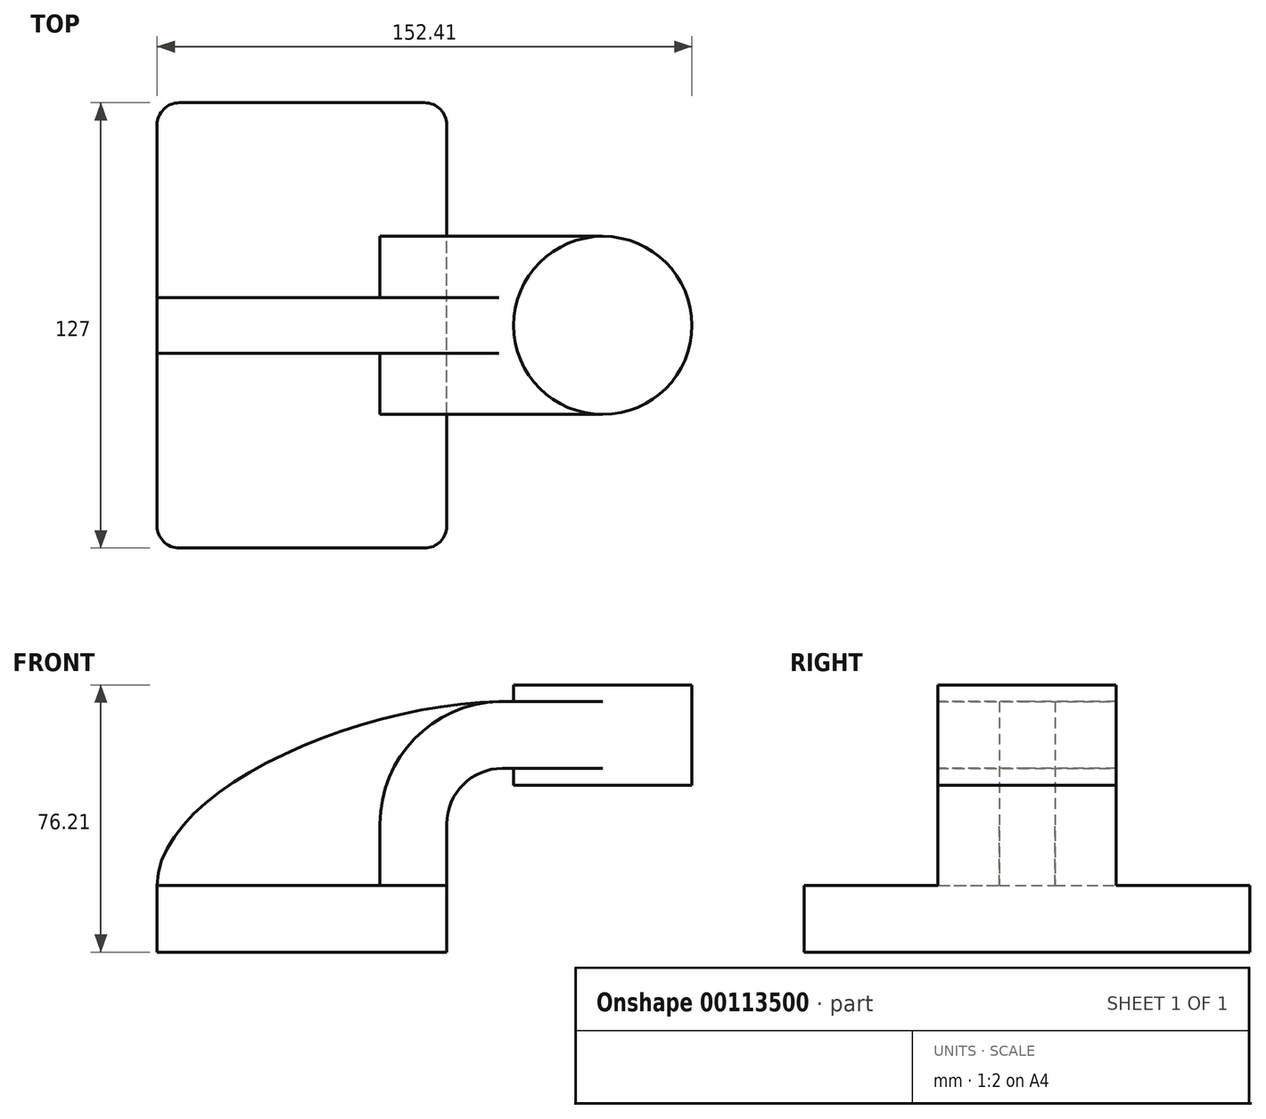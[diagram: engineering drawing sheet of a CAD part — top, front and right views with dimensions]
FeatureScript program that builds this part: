
annotation { "Feature Type Name" : "Feature", "Feature Type Description" : "" }
export const myFeature = defineFeature(function(context is Context, id is Id, definition is map)
    precondition{}
    {
        {
            var Q0;
            Q0=qCreatedBy(makeId("Front.planeOp"),FACE);
            var sketch = newSketch(context, id + "F0", { "sketchPlane" : qUnion([Q0])});
            skLineSegment(sketch, "E0.bottom", {"start": v(41.28, -9.53) * mm, "end": v(-41.28, -9.53) * mm});
            skLineSegment(sketch, "E0.top", {"start": v(41.28, 9.53) * mm, "end": v(-41.28, 9.53) * mm});
            skLineSegment(sketch, "E0.left", {"start": v(41.28, -9.53) * mm, "end": v(41.28, 9.53) * mm});
            skLineSegment(sketch, "E0.right", {"start": v(-41.28, -9.53) * mm, "end": v(-41.28, 9.53) * mm});
            skPoint(sketch, "E0.middle", {"position": v(0, 0) * mm});
            skLineSegment(sketch, "E1.bottom", {"start": v(60.32, 66.67) * mm, "end": v(111.12, 66.67) * mm});
            skLineSegment(sketch, "E1.top", {"start": v(60.32, 38.1) * mm, "end": v(111.12, 38.1) * mm});
            skLineSegment(sketch, "E1.left", {"start": v(60.32, 66.68) * mm, "end": v(60.32, 38.1) * mm});
            skLineSegment(sketch, "E1.right", {"start": v(111.12, 66.68) * mm, "end": v(111.12, 38.1) * mm});
            skPoint(sketch, "E1.middle", {"position": v(85.72, 52.39) * mm});
            skLineSegment(sketch, "E2", {"start": v(41.28, 9.53) * mm, "end": v(41.28, 27) * mm});
            skArc(sketch, "E3", {"start": v(41.28, 27) * mm, "mid": v(45.92, 38.23) * mm, "end": v(57.15, 42.88) * mm});
            skLineSegment(sketch, "E4", {"start": v(57.15, 42.88) * mm, "end": v(85.72, 42.88) * mm});
            skPoint(sketch, "E5", {"position": v(85.72, 38.1) * mm});
            skLineSegment(sketch, "E6.0", {"start": v(57.15, 61.93) * mm, "end": v(88.2, 61.93) * mm});
            skArc(sketch, "E6.1", {"start": v(22.23, 27) * mm, "mid": v(32.45, 51.7) * mm, "end": v(57.15, 61.93) * mm});
            skLineSegment(sketch, "E6.2", {"start": v(22.23, 9.52) * mm, "end": v(22.23, 27) * mm});
            skLineSegment(sketch, "E7", {"start": v(85.72, 38.1) * mm, "end": v(85.72, 66.68) * mm});
            skFitSpline(sketch, "E8", {"points": [v(57.15, 61.93) * mm, v(-41.28, 9.52) * mm], "startDerivative": vector(-122, -1.2) * mm, "endDerivative": vector(-0.88, -82.44) * mm});
            skSolve(sketch);
        }
        {
            var Q0;
            Q0=makeQuery(id+"F0.imprint","IMPRINT",FACE,{"disambiguationData":[TD([[makeQuery(id+"F0.imprint","IMPRINT",EDGE,{"derivedFrom":sQuery(id+"F0.wireOp",EDGE,"E0.bottom")}),-1.0]])]});
            extrude(context, id + "F1", {"entities" : qUnion([Q0]), "endBound" : BoundingType.SYMMETRIC, "depth" : 127 * mm});
        }
        {
            var Q0;
            {var subQ0=sQuery(id+"F0.wireOp",EDGE,"E6.0");var subQ1=sQuery(id+"F0.wireOp",EDGE,"E1.left");var subQ2=makeQuery(id+"F0.imprint","INTERSECT",VERTEX,{"derivedFrom":[subQ1,subQ0]});Q0=makeQuery(id+"F0.imprint","IMPRINT",FACE,{"disambiguationData":[TD([[makeQuery(id+"F0.imprint","IMPRINT",EDGE,{"disambiguationData":[TD([[subQ2,-1.0]])],"derivedFrom":subQ1}),1.0]])]});}
            var Q1;
            {var subQ6=sQuery(id+"F0.wireOp",EDGE,"E2");Q1=makeQuery(id+"F0.imprint","IMPRINT",FACE,{"disambiguationData":[TD([[makeQuery(id+"F0.imprint","IMPRINT",EDGE,{"derivedFrom":subQ6}),1.0]])]});}
            extrude(context, id + "F2", {"entities" : qUnion([Q0, Q1]), "operationType" : NewBodyOperationType.ADD, "endBound" : BoundingType.SYMMETRIC, "depth" : 50.8 * mm});
        }
        {
            var Q0;
            {var subQ3=sQuery(id+"F0.wireOp",EDGE,"E6.2");Q0=makeQuery(id+"F0.imprint","IMPRINT",FACE,{"disambiguationData":[TD([[makeQuery(id+"F0.imprint","IMPRINT",EDGE,{"derivedFrom":subQ3}),1.0]])]});}
            extrude(context, id + "F3", {"entities" : qUnion([Q0]), "operationType" : NewBodyOperationType.ADD, "endBound" : BoundingType.SYMMETRIC, "depth" : 15.88 * mm});
        }
        {
            var Q0;
            {var subQ0=sQuery(id+"F0.wireOp",EDGE,"E1.right");Q0=makeQuery(id+"F0.imprint","IMPRINT",FACE,{"disambiguationData":[TD([[makeQuery(id+"F0.imprint","IMPRINT",EDGE,{"derivedFrom":subQ0}),-1.0]])]});}
            var Q1;
            Q1=sQuery(id+"F0.wireOp",EDGE,"E7");
            revolve(context, id + "F4", {"operationType" : NewBodyOperationType.ADD, "entities" : qUnion([Q0]), "axis" : qUnion([Q1]), "revolveType" : RevolveType.FULL});
        }
        {
            var Q0;
            Q0=makeQuery(id+"F1.opExtrude","CAP_EDGE",EDGE,{"disambiguationData":[OSD([sQuery(id+"F0.wireOp",EDGE,"E0.right")])],"isStart":true});
            var Q1;
            Q1=makeQuery(id+"F1.opExtrude","CAP_EDGE",EDGE,{"disambiguationData":[OSD([sQuery(id+"F0.wireOp",EDGE,"E0.left")])],"isStart":true});
            var Q2;
            Q2=makeQuery(id+"F1.opExtrude","CAP_EDGE",EDGE,{"disambiguationData":[OSD([sQuery(id+"F0.wireOp",EDGE,"E0.right")])],"isStart":false});
            var Q3;
            Q3=makeQuery(id+"F1.opExtrude","CAP_EDGE",EDGE,{"disambiguationData":[OSD([sQuery(id+"F0.wireOp",EDGE,"E0.left")])],"isStart":false});
            fillet(context, id + "F5", {"entities" : qUnion([Q0, Q1, Q2, Q3]), "radius" : 6.35 * mm, "tangentPropagation" : true, "allowEdgeOverflow" : false});
        }
    });
